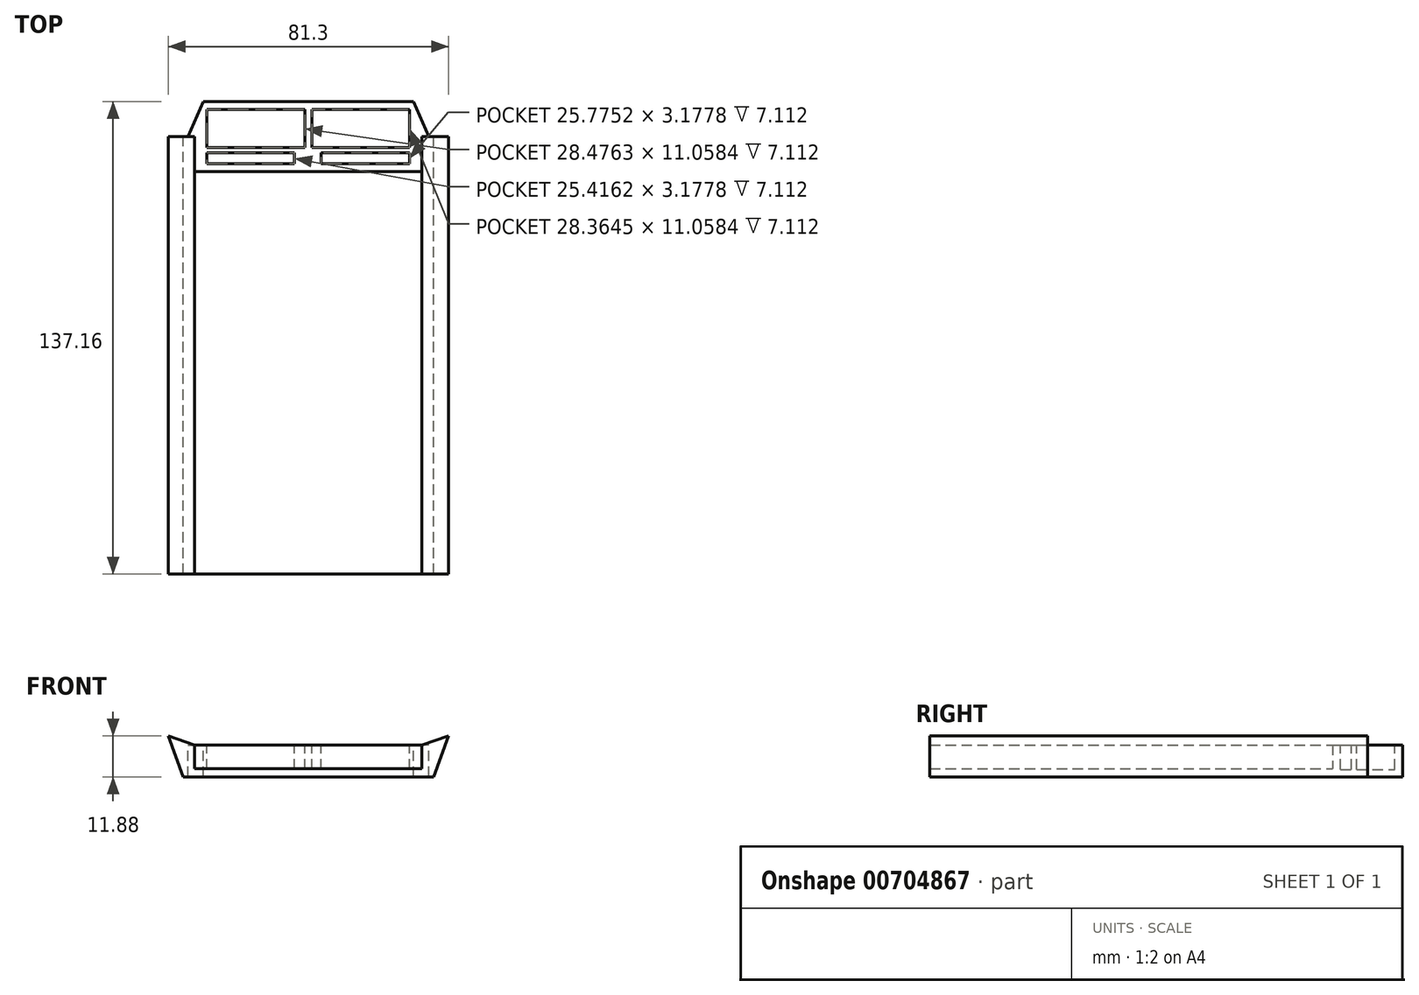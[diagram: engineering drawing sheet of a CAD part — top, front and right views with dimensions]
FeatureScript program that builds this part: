
annotation { "Feature Type Name" : "Feature", "Feature Type Description" : "" }
export const myFeature = defineFeature(function(context is Context, id is Id, definition is map)
    precondition{}
    {
        {
            var Q0;
            Q0=qCreatedBy(makeId("Front.planeOp"),FACE);
            var sketch = newSketch(context, id + "F0", { "sketchPlane" : qUnion([Q0])});
            skLineSegment(sketch, "E0.top", {"start": v(-36.28, -5.94) * mm, "end": v(36.28, -5.94) * mm});
            skPoint(sketch, "E0.middle", {"position": v(0, 0) * mm});
            skLineSegment(sketch, "E1", {"start": v(-40.65, 5.94) * mm, "end": v(-36.28, -5.94) * mm});
            skLineSegment(sketch, "E2", {"start": v(-40.65, 5.94) * mm, "end": v(-32.94, 3.35) * mm});
            skLineSegment(sketch, "E3", {"start": v(-32.94, 3.35) * mm, "end": v(-32.94, -3.55) * mm});
            skLineSegment(sketch, "E4", {"start": v(-32.94, -3.55) * mm, "end": v(0, -3.55) * mm});
            skLineSegment(sketch, "E5.MirrorCS", {"start": v(40.65, 5.94) * mm, "end": v(36.28, -5.94) * mm});
            skLineSegment(sketch, "E6.MirrorCS", {"start": v(40.65, 5.94) * mm, "end": v(32.94, 3.35) * mm});
            skLineSegment(sketch, "E7.MirrorCS", {"start": v(32.94, 3.35) * mm, "end": v(32.94, -3.55) * mm});
            skLineSegment(sketch, "E8.MirrorCS", {"start": v(32.94, -3.55) * mm, "end": v(0, -3.55) * mm});
            skPoint(sketch, "E9.orphan", {"position": v(-40.65, -5.94) * mm});
            skPoint(sketch, "E0.right.start.orphan", {"position": v(40.65, 5.94) * mm});
            skPoint(sketch, "E10.orphan", {"position": v(40.65, -5.94) * mm});
            skSolve(sketch);
        }
        {
            var Q0;
            Q0 = qSketchRegion(id + "F0", true);
            extrude(context, id + "F1", {"entities" : qUnion([Q0]), "depth" : 127 * mm, "offsetDistance" : 25.4 * mm});
        }
        {
            var Q0;
            Q0=makeQuery(id+"F1.opExtrude","CAP_FACE",FACE,{"disambiguationData":[OSD([sQuery(id+"F0.wireOp",EDGE,"E0.top"),sQuery(id+"F0.wireOp",EDGE,"E1"),sQuery(id+"F0.wireOp",EDGE,"E2"),sQuery(id+"F0.wireOp",EDGE,"E3"),sQuery(id+"F0.wireOp",EDGE,"E4"),sQuery(id+"F0.wireOp",EDGE,"E5.MirrorCS"),sQuery(id+"F0.wireOp",EDGE,"E6.MirrorCS"),sQuery(id+"F0.wireOp",EDGE,"E7.MirrorCS"),sQuery(id+"F0.wireOp",EDGE,"E8.MirrorCS")])],"isStart":true});
            var sketch = newSketch(context, id + "F2", { "sketchPlane" : qUnion([Q0])});
            skLineSegment(sketch, "E11.bottom", {"start": v(-34.91, -5.94) * mm, "end": v(34.91, -5.94) * mm});
            skLineSegment(sketch, "E11.left", {"start": v(-34.91, -5.94) * mm, "end": v(-34.91, 3.35) * mm});
            skLineSegment(sketch, "E11.right", {"start": v(34.91, -5.94) * mm, "end": v(34.91, 3.35) * mm});
            skPoint(sketch, "E11.middle", {"position": v(0, 0) * mm});
            skLineSegment(sketch, "E12", {"start": v(-32.94, 3.35) * mm, "end": v(34.91, 3.35) * mm});
            skLineSegment(sketch, "E13", {"start": v(34.91, 3.35) * mm, "end": v(-32.94, 3.35) * mm});
            skLineSegment(sketch, "E14", {"start": v(-32.94, 3.35) * mm, "end": v(-34.91, 3.35) * mm});
            skPoint(sketch, "E15.orphan", {"position": v(-34.91, 5.94) * mm});
            skPoint(sketch, "E16.orphan", {"position": v(34.91, 5.94) * mm});
            skSolve(sketch);
        }
        {
            var Q0;
            Q0 = qSketchRegion(id + "F2", true);
            extrude(context, id + "F3", {"entities" : qUnion([Q0]), "operationType" : NewBodyOperationType.ADD, "depth" : 10.16 * mm, "offsetDistance" : 25.4 * mm});
        }
        {
            var Q0;
            Q0=makeQuery(id+"F3.opExtrude","CAP_FACE",FACE,{"disambiguationData":[OSD([sQuery(id+"F2.wireOp",EDGE,"E11.bottom"),sQuery(id+"F2.wireOp",EDGE,"E11.left"),sQuery(id+"F2.wireOp",EDGE,"E11.right"),sQuery(id+"F2.wireOp",EDGE,"E13"),sQuery(id+"F2.wireOp",EDGE,"E14")])],"isStart":true});
            var sketch = newSketch(context, id + "F4", { "sketchPlane" : qUnion([Q0])});
            skLineSegment(sketch, "E17.bottom", {"start": v(32.94, -3.55) * mm, "end": v(-32.94, -3.55) * mm});
            skLineSegment(sketch, "E17.top", {"start": v(32.94, 3.35) * mm, "end": v(-32.94, 3.35) * mm});
            skLineSegment(sketch, "E17.left", {"start": v(32.94, -3.55) * mm, "end": v(32.94, 3.35) * mm});
            skLineSegment(sketch, "E17.right", {"start": v(-32.94, -3.55) * mm, "end": v(-32.94, 3.35) * mm});
            skSolve(sketch);
        }
        {
            var Q0;
            Q0 = qSketchRegion(id + "F4", true);
            extrude(context, id + "F5", {"entities" : qUnion([Q0]), "operationType" : NewBodyOperationType.ADD, "depth" : 10.16 * mm, "offsetDistance" : 25.4 * mm});
        }
        {
            var Q0;
            Q0=makeQuery(id+"F5.boolean.opBoolean","MERGE",FACE,{"derivedFrom":[makeQuery(id+"F3.opExtrude","SWEPT_FACE",FACE,{"disambiguationData":[OSD([sQuery(id+"F2.wireOp",EDGE,"E13"),sQuery(id+"F2.wireOp",EDGE,"E14")])]}),makeQuery(id+"F5.opExtrude","SWEPT_FACE",FACE,{"disambiguationData":[OSD([sQuery(id+"F4.wireOp",EDGE,"E17.top")])]})]});
            var sketch = newSketch(context, id + "F6", { "sketchPlane" : qUnion([Q0])});
            skLineSegment(sketch, "E18", {"start": v(34.91, 0) * mm, "end": v(30.48, 10.16) * mm});
            skLineSegment(sketch, "E19", {"start": v(0, 0) * mm, "end": v(0, 16.13) * mm, "construction": true});
            skLineSegment(sketch, "E20.MirrorCS", {"start": v(-34.91, 0) * mm, "end": v(-30.48, 10.16) * mm});
            skLineSegment(sketch, "E21", {"start": v(30.48, 10.16) * mm, "end": v(34.91, 10.16) * mm});
            skLineSegment(sketch, "E22", {"start": v(34.91, 10.16) * mm, "end": v(34.91, 0) * mm});
            skLineSegment(sketch, "E23.MirrorCS", {"start": v(-30.48, 10.16) * mm, "end": v(-34.91, 10.16) * mm});
            skLineSegment(sketch, "E24.MirrorCS", {"start": v(-34.91, 10.16) * mm, "end": v(-34.91, 0) * mm});
            skSolve(sketch);
        }
        {
            var Q0;
            Q0 = qSketchRegion(id + "F6", true);
            extrude(context, id + "F7", {"entities" : qUnion([Q0]), "operationType" : NewBodyOperationType.REMOVE, "oppositeDirection" : true, "depth" : 25.4 * mm, "offsetDistance" : 25.4 * mm});
        }
        {
            var Q0;
            Q0=makeQuery(id+"F5.boolean.opBoolean","MERGE",FACE,{"derivedFrom":[makeQuery(id+"F3.opExtrude","SWEPT_FACE",FACE,{"disambiguationData":[OSD([sQuery(id+"F2.wireOp",EDGE,"E13"),sQuery(id+"F2.wireOp",EDGE,"E14")])]}),makeQuery(id+"F5.opExtrude","SWEPT_FACE",FACE,{"disambiguationData":[OSD([sQuery(id+"F4.wireOp",EDGE,"E17.top")])]})]});
            var sketch = newSketch(context, id + "F8", { "sketchPlane" : qUnion([Q0])});
            skLineSegment(sketch, "E25.bottom", {"start": v(29.42, -7.88) * mm, "end": v(3.65, -7.88) * mm});
            skLineSegment(sketch, "E25.top", {"start": v(29.42, 7.88) * mm, "end": v(1.06, 7.88) * mm});
            skLineSegment(sketch, "E25.left", {"start": v(29.42, -7.88) * mm, "end": v(29.42, -4.7) * mm});
            skLineSegment(sketch, "E25.right", {"start": v(-29.42, -7.88) * mm, "end": v(-29.42, -4.7) * mm});
            skPoint(sketch, "E25.middle", {"position": v(0, 0) * mm});
            skLineSegment(sketch, "E26", {"start": v(29.42, -4.7) * mm, "end": v(3.65, -4.7) * mm});
            skLineSegment(sketch, "E27", {"start": v(29.42, -3.18) * mm, "end": v(1.06, -3.18) * mm});
            skLineSegment(sketch, "E28.trimOffspring", {"start": v(29.42, -3.18) * mm, "end": v(29.42, 7.88) * mm});
            skLineSegment(sketch, "E29.trimOffspring", {"start": v(-29.42, -3.18) * mm, "end": v(-29.42, 7.88) * mm});
            skLineSegment(sketch, "E30.top", {"start": v(3.65, -3.18) * mm, "end": v(1.06, -3.18) * mm});
            skLineSegment(sketch, "E30.left", {"start": v(3.65, -7.88) * mm, "end": v(3.65, -4.7) * mm});
            skLineSegment(sketch, "E30.right", {"start": v(-4, -7.88) * mm, "end": v(-4, -4.7) * mm});
            skLineSegment(sketch, "E31.left", {"start": v(1.06, -3.18) * mm, "end": v(1.06, 7.88) * mm});
            skLineSegment(sketch, "E31.right", {"start": v(-0.94, -3.18) * mm, "end": v(-0.94, 7.88) * mm});
            skLineSegment(sketch, "E32.trimOffspring", {"start": v(-4, -4.7) * mm, "end": v(-29.42, -4.7) * mm});
            skLineSegment(sketch, "E33.trimOffspring", {"start": v(-0.94, -3.18) * mm, "end": v(-4, -3.18) * mm});
            skLineSegment(sketch, "E34.trimOffspring", {"start": v(-0.94, -3.18) * mm, "end": v(-29.42, -3.18) * mm});
            skLineSegment(sketch, "E35.trimOffspring", {"start": v(-4, -7.88) * mm, "end": v(-29.42, -7.88) * mm});
            skLineSegment(sketch, "E36.trimOffspring", {"start": v(-0.94, 7.88) * mm, "end": v(-29.42, 7.88) * mm});
            skSolve(sketch);
        }
        {
            var Q0;
            Q0 = qSketchRegion(id + "F8", true);
            extrude(context, id + "F9", {"entities" : qUnion([Q0]), "operationType" : NewBodyOperationType.REMOVE, "oppositeDirection" : true, "depth" : 7.11 * mm, "offsetDistance" : 25.4 * mm});
        }
    });
